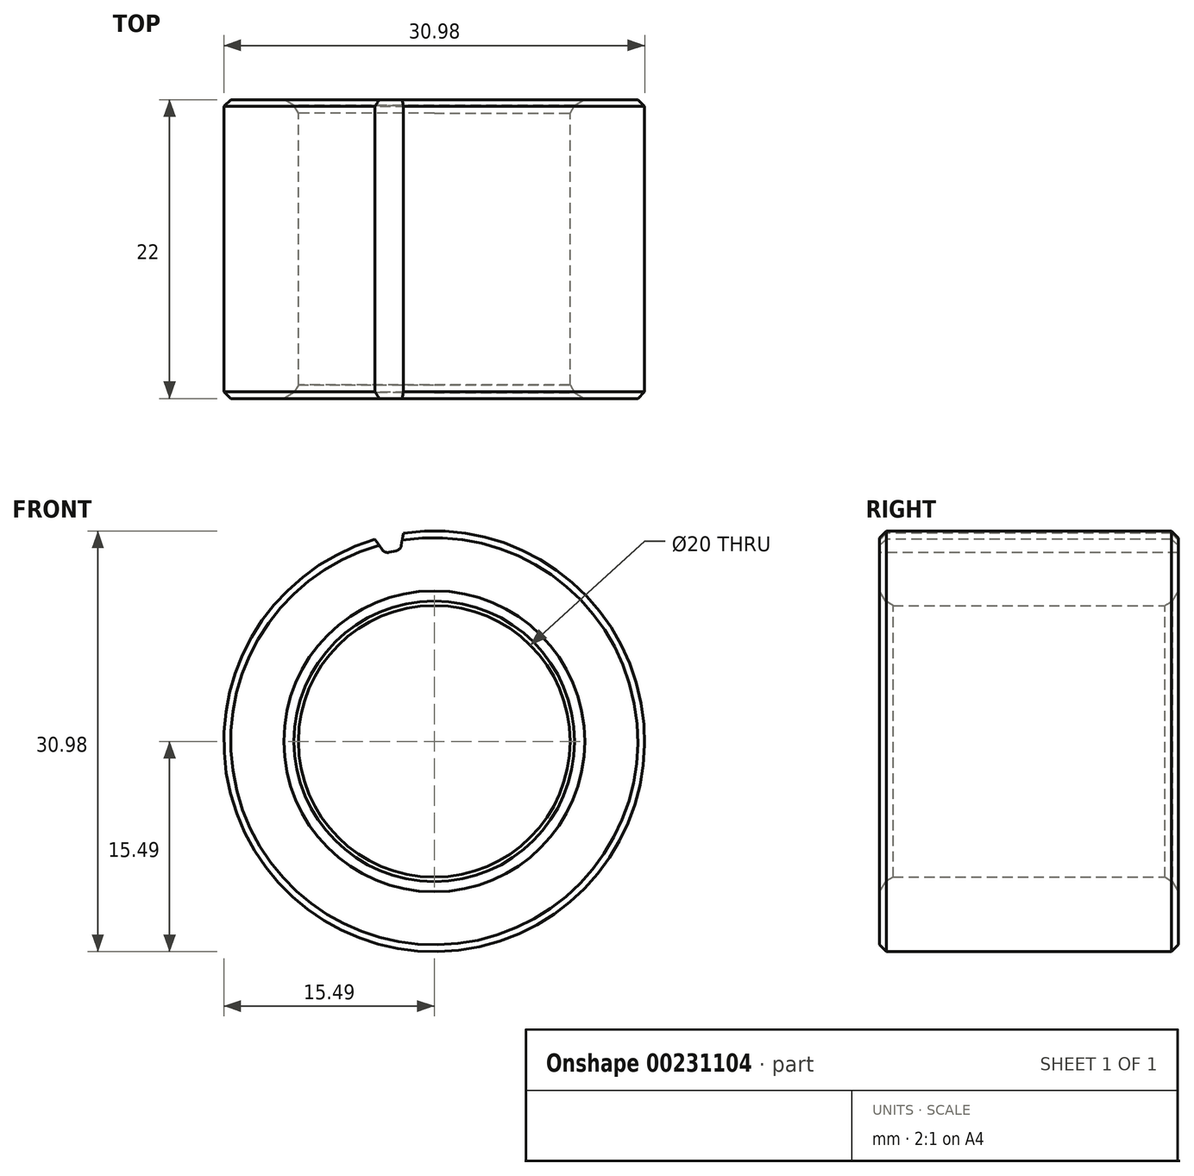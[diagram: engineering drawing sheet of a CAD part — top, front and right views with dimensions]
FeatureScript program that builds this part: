
annotation { "Feature Type Name" : "Feature", "Feature Type Description" : "" }
export const myFeature = defineFeature(function(context is Context, id is Id, definition is map)
    precondition{}
    {
        {
            var Q0;
            Q0=qCreatedBy(makeId("Front.planeOp"),FACE);
            var sketch = newSketch(context, id + "F0", { "sketchPlane" : qUnion([Q0])});
            skCircle(sketch, "E0", {"center": v(0, 0) * mm, "radius": 10 * mm});
            skCircle(sketch, "E1", {"center": v(0, 0) * mm, "radius": 15.49 * mm});
            skSolve(sketch);
        }
        {
            var Q0;
            Q0=makeQuery(id+"F0.imprint","IMPRINT",FACE,{"disambiguationData":[TD([[makeQuery(id+"F0.imprint","IMPRINT",EDGE,{"derivedFrom":sQuery(id+"F0.wireOp",EDGE,"E0")}),-1.0]])]});
            extrude(context, id + "F1", {"entities" : qUnion([Q0]), "endBound" : BoundingType.SYMMETRIC, "depth" : 22 * mm});
        }
        {
            var Q0;
            Q0=makeQuery(id+"F1.opExtrude","CAP_EDGE",EDGE,{"disambiguationData":[OSD([sQuery(id+"F0.wireOp",EDGE,"E0")])],"isStart":false});
            var Q1;
            Q1=makeQuery(id+"F1.opExtrude","CAP_EDGE",EDGE,{"disambiguationData":[OSD([sQuery(id+"F0.wireOp",EDGE,"E0")])],"isStart":true});
            chamfer(context, id + "F2", {"entities" : qUnion([Q0, Q1]), "chamferType" : ChamferType.OFFSET_ANGLE, "width" : 1 * mm, "oppositeDirection" : false, "angle" : 30 * degree, "tangentPropagation" : true});
        }
        {
            var Q0;
            {var subQ0=sQuery(id+"F0.wireOp",EDGE,"E0");Q0=makeQuery(id+"F2.opChamfer","BLEND_EDGE",EDGE,{"blendedFrom":[makeQuery(id+"F1.opExtrude","CAP_EDGE",EDGE,{"disambiguationData":[OSD([subQ0])],"isStart":false}),makeQuery(id+"F1.opExtrude","CAP_FACE",FACE,{"disambiguationData":[OSD([subQ0,sQuery(id+"F0.wireOp",EDGE,"E1")])],"isStart":false})],"blendedInto":[makeQuery(id+"F1.opExtrude","CAP_FACE",FACE,{"disambiguationData":[OSD([subQ0,sQuery(id+"F0.wireOp",EDGE,"E1")])],"isStart":false})]});}
            var Q1;
            {var subQ0=sQuery(id+"F0.wireOp",EDGE,"E0");Q1=makeQuery(id+"F2.opChamfer","BLEND_EDGE",EDGE,{"blendedFrom":[makeQuery(id+"F1.opExtrude","CAP_EDGE",EDGE,{"disambiguationData":[OSD([subQ0])],"isStart":true}),makeQuery(id+"F1.opExtrude","CAP_FACE",FACE,{"disambiguationData":[OSD([subQ0,sQuery(id+"F0.wireOp",EDGE,"E1")])],"isStart":true})],"blendedInto":[makeQuery(id+"F1.opExtrude","CAP_FACE",FACE,{"disambiguationData":[OSD([subQ0,sQuery(id+"F0.wireOp",EDGE,"E1")])],"isStart":true})]});}
            chamfer(context, id + "F3", {"entities" : qUnion([Q0, Q1]), "chamferType" : ChamferType.TWO_OFFSETS, "width1" : 0.5 * mm, "oppositeDirection" : false, "width2" : 0.5 * mm, "tangentPropagation" : true});
        }
        {
            var Q0;
            Q0=qCreatedBy(makeId("Front.planeOp"),FACE);
            var sketch = newSketch(context, id + "F4", { "sketchPlane" : qUnion([Q0])});
            skArc(sketch, "E2.0", {"start": v(-2.27, 15.32) * mm, "mid": v(-3.32, 15.12) * mm, "end": v(-4.36, 14.86) * mm});
            skLineSegment(sketch, "E3", {"start": v(-2.27, 15.32) * mm, "end": v(-2.43, 14.42) * mm});
            skLineSegment(sketch, "E4", {"start": v(-2.81, 14.02) * mm, "end": v(-3.32, 13.91) * mm});
            skLineSegment(sketch, "E5", {"start": v(-3.83, 14.11) * mm, "end": v(-4.36, 14.86) * mm});
            skPoint(sketch, "E6.visualSharp", {"position": v(-2.48, 14.09) * mm});
            skArc(sketch, "E6.filletArc", {"start": v(-2.81, 14.02) * mm, "mid": v(-2.56, 14.16) * mm, "end": v(-2.43, 14.42) * mm});
            skPoint(sketch, "E7.visualSharp", {"position": v(-3.64, 13.84) * mm});
            skArc(sketch, "E7.filletArc", {"start": v(-3.83, 14.11) * mm, "mid": v(-3.6, 13.94) * mm, "end": v(-3.32, 13.91) * mm});
            skSolve(sketch);
        }
        {
            var Q0;
            Q0=makeQuery(id+"F4.imprint","IMPRINT",FACE,{"disambiguationData":[TD([[makeQuery(id+"F4.imprint","IMPRINT",EDGE,{"derivedFrom":sQuery(id+"F4.wireOp",EDGE,"E2.0")}),1.0]])]});
            extrude(context, id + "F5", {"entities" : qUnion([Q0]), "operationType" : NewBodyOperationType.REMOVE, "endBound" : BoundingType.SYMMETRIC, "oppositeDirection" : true, "depth" : 25 * mm});
        }
        {
            var Q0;
            Q0=makeQuery(id+"F1.opExtrude","CAP_EDGE",EDGE,{"disambiguationData":[OSD([sQuery(id+"F0.wireOp",EDGE,"E1")])],"isStart":true});
            var Q1;
            Q1=makeQuery(id+"F1.opExtrude","CAP_EDGE",EDGE,{"disambiguationData":[OSD([sQuery(id+"F0.wireOp",EDGE,"E1")])],"isStart":false});
            chamfer(context, id + "F6", {"entities" : qUnion([Q0, Q1]), "chamferType" : ChamferType.OFFSET_ANGLE, "width" : 0.5 * mm, "oppositeDirection" : false, "angle" : 45 * degree, "tangentPropagation" : true});
        }
    });
